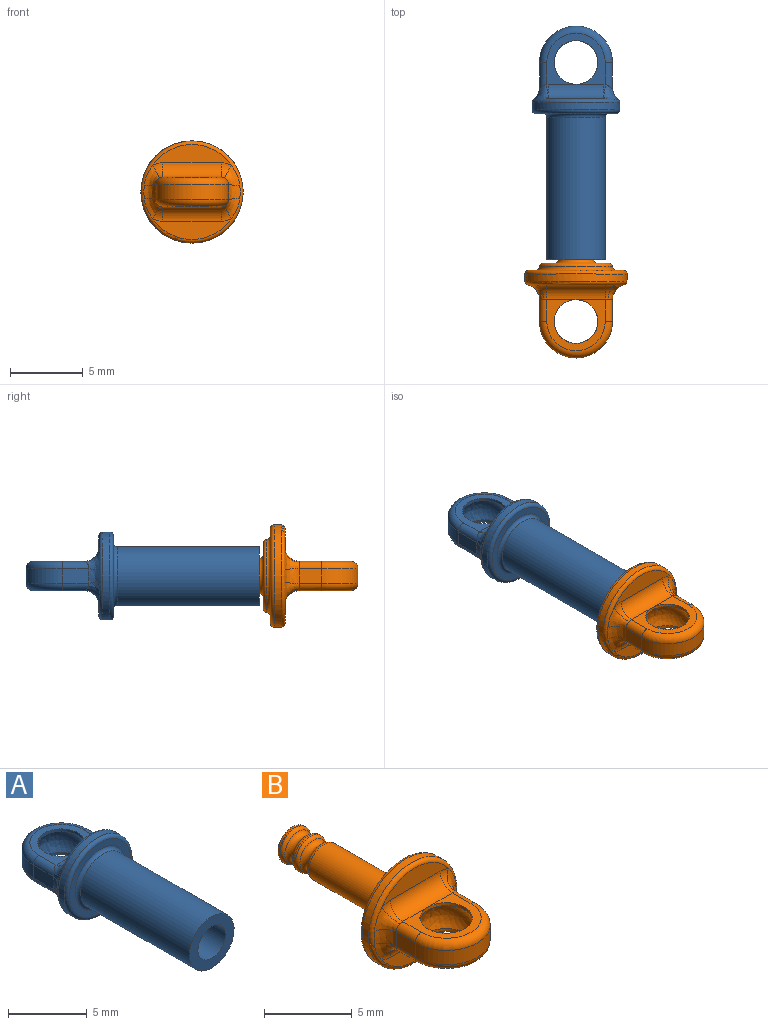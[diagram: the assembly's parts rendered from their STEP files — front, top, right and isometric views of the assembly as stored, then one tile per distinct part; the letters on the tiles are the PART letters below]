
ASSEMBLY  parts=2 mates=1
PART A: 38 faces, bbox 6.5x16.2x6.5 mm
  f0: plane 3.78x0.75mm, normal (0,1,0), area 1.9mm2, adj f23,f35
  f1: cylinder r=1.5mm len=3mm, axis (0,0,-1), area 1.9mm2, adj f7,f8
  f2: plane 1.78x1mm, normal (1,0,0), area 1.8mm2, adj f3,f11,f14,f32
  f3: cylinder r=2.5mm len=5mm, axis (0,0,-1), area 7.9mm2, adj f2,f4,f10,f13
  f4: plane 1.78x1mm, normal (-1,0,0), area 1.8mm2, adj f3,f9,f12,f29
  f5: cylinder r=1.5mm len=3mm, axis (0,0,-1), area 1.9mm2, adj f6,f8
  f6: plane 4x3.5mm, normal (0,0,1), area 5.2mm2, adj f5,f12,f13,f14,f33,f35,f36
  f7: plane 4x3.5mm, normal (0,0,-1), area 5.2mm2, adj f1,f9,f10,f11,f25,f26,f28
  f8: sphere r=1.7mm, area 17.1mm2, adj f1,f5
  f9: cylinder r=0.5mm len=1.78mm, axis (0,-1,0), area 1.3mm2, adj f4,f7,f10,f27
  f10: torus R=2mm, axis (0,0,1), area 5.7mm2, adj f3,f7,f9,f11
  f11: cylinder r=0.5mm len=1.78mm, axis (0,1,0), area 1.3mm2, adj f2,f7,f10,f30
  f12: cylinder r=0.5mm len=1.78mm, axis (0,1,0), area 1.3mm2, adj f4,f6,f13,f31
  f13: torus R=2mm, axis (0,0,1), area 5.7mm2, adj f3,f6,f12,f14
  f14: cylinder r=0.5mm len=1.78mm, axis (0,-1,0), area 1.3mm2, adj f2,f6,f13,f34
  f15: plane 3.78x0.75mm, normal (0,1,0), area 1.9mm2, adj f23,f26
  f16: cylinder r=3mm len=6mm, axis (0,1,0), area 9.4mm2, adj f23,f24
  f17: plane 0.48x0.48mm, normal (0,-1,0), area 0.2mm2, adj f18
  f18: torus R=0.24mm, axis (0,1,0), area 8.7mm2, adj f17,f19
  f19: cylinder r=1.24mm len=9mm, axis (0,1,0), area 70.2mm2, adj f18,f20
  f20: plane 4x4mm, normal (0,-1,0), area 7.7mm2, adj f19,f21
  f21: cylinder r=2mm len=9.75mm, axis (0,1,0), area 122.5mm2, adj f20,f37
  f22: plane 5.5x5.5mm, normal (0,-1,0), area 7.9mm2, adj f24,f37
  f23: torus R=2.75mm, axis (0,-1,0), area 6mm2, adj f0,f15,f16,f25,f27,f28,f29,f30
  f24: torus R=2.75mm, axis (0,1,0), area 7.2mm2, adj f16,f22
  f25: bspline ~1.1x1.1mm, area 0.1mm2, adj f7,f23,f26,f27
  f26: cylinder r=1mm len=3.78mm, axis (1,0,0), area 5.9mm2, adj f7,f15,f25,f28
  f27: bspline ~1.82x1.08mm, area 1.2mm2, adj f9,f23,f25,f29
  f28: bspline ~1.1x1.1mm, area 0.1mm2, adj f7,f23,f26,f30
  f29: bspline ~1.56x0.82mm, area 0.8mm2, adj f4,f23,f27,f31
  f30: bspline ~1.76x1.09mm, area 1.2mm2, adj f11,f23,f28,f32
  f31: bspline ~1.76x1.09mm, area 1.2mm2, adj f12,f23,f29,f33
  f32: bspline ~1.46x0.81mm, area 0.8mm2, adj f2,f23,f30,f34
  f33: bspline ~1.1x1.1mm, area 0.1mm2, adj f6,f23,f31,f35
  f34: bspline ~1.82x1.08mm, area 1.2mm2, adj f14,f23,f32,f36
  f35: cylinder r=1mm len=3.78mm, axis (-1,0,0), area 5.9mm2, adj f0,f6,f33,f36
  f36: bspline ~1.1x1.1mm, area 0.1mm2, adj f6,f23,f34,f35
  f37: torus R=2.25mm, axis (0,1,0), area 5.2mm2, adj f21,f22
PART B: 47 faces, bbox 7.6x15.2x7.6 mm
  f0: cylinder r=1.5mm len=3mm, axis (0,0,-1), area 1.9mm2, adj f22,f46
  f1: plane 5.36x1.41mm, normal (0,-1,0), area 4.5mm2, adj f29,f43,f44,f45
  f2: plane 5.36x1.41mm, normal (0,-1,0), area 4.5mm2, adj f29,f34,f35,f36
  f3: cylinder r=3.5mm len=7mm, axis (0,1,0), area 11mm2, adj f29,f30
  f4: plane 6.5x6.5mm, normal (0,1,0), area 9.4mm2, adj f30,f32
  f5: plane 4.5x4.5mm, normal (0,1,0), area 9.3mm2, adj f31,f33
  f6: cylinder r=1.2mm len=5.62mm, axis (0,1,0), area 42.4mm2, adj f7,f33
  f7: torus R=0.95mm, axis (0,1,0), area 2.1mm2, adj f6,f8
  f8: torus R=1.2mm, axis (0,1,0), area 4.6mm2, adj f7,f9
  f9: torus R=0.95mm, axis (0,1,0), area 2.1mm2, adj f8,f10
  f10: cylinder r=1.2mm len=2.4mm, axis (0,1,0), area 0.9mm2, adj f9,f11
  f11: torus R=0.95mm, axis (0,1,0), area 2.1mm2, adj f10,f12
  f12: torus R=1.2mm, axis (0,1,0), area 4.6mm2, adj f11,f13
  f13: torus R=0.95mm, axis (0,1,0), area 2.1mm2, adj f12,f14
  f14: cylinder r=1.2mm len=2.4mm, axis (0,1,0), area 0.6mm2, adj f13,f15
  f15: torus R=0.95mm, axis (0,1,0), area 2.7mm2, adj f14,f16
  f16: plane 1.9x1.9mm, normal (0,1,0), area 2.8mm2, adj f15
  f17: plane 1.53x1mm, normal (-1,0,0), area 1.5mm2, adj f18,f23,f26,f39
  f18: cylinder r=2.5mm len=5mm, axis (0,0,-1), area 7.9mm2, adj f17,f19,f24,f27
  f19: plane 1.53x1mm, normal (1,0,0), area 1.5mm2, adj f18,f25,f28,f40
  f20: cylinder r=1.5mm len=3mm, axis (0,0,-1), area 1.9mm2, adj f21,f46
  f21: plane 4x3.5mm, normal (0,0,1), area 5.2mm2, adj f20,f26,f27,f28,f34
  f22: plane 4x3.5mm, normal (0,0,-1), area 5.2mm2, adj f0,f23,f24,f25,f45
  f23: cylinder r=0.5mm len=1.53mm, axis (0,-1,0), area 1.2mm2, adj f17,f22,f24,f41,f43
  f24: torus R=2mm, axis (0,0,1), area 5.7mm2, adj f18,f22,f23,f25
  f25: cylinder r=0.5mm len=1.53mm, axis (0,1,0), area 1.2mm2, adj f19,f22,f24,f42,f44
  f26: cylinder r=0.5mm len=1.53mm, axis (0,1,0), area 1.2mm2, adj f17,f21,f27,f35,f37
  f27: torus R=2mm, axis (0,0,1), area 5.7mm2, adj f18,f21,f26,f28
  f28: cylinder r=0.5mm len=1.53mm, axis (0,-1,0), area 1.2mm2, adj f19,f21,f27,f36,f38
  f29: torus R=3.25mm, axis (0,1,0), area 8mm2, adj f1,f2,f3,f37,f38,f39,f40,f41
  f30: torus R=3.25mm, axis (0,-1,0), area 8.4mm2, adj f3,f4
  f31: torus R=2.25mm, axis (0,-1,0), area 5.9mm2, adj f5,f32
  f32: torus R=2.75mm, axis (0,-1,0), area 6.4mm2, adj f4,f31
  f33: torus R=1.45mm, axis (0,-1,0), area 3.2mm2, adj f5,f6
  f34: cylinder r=1mm len=4mm, axis (1,0,0), area 6.3mm2, adj f2,f21,f35,f36
  f35: torus R=1.5mm, axis (0,1,0), area 0.6mm2, adj f2,f26,f34,f37
  f36: torus R=1.5mm, axis (0,1,0), area 0.6mm2, adj f2,f28,f34,f38
  f37: bspline ~1.87x1.16mm, area 1.2mm2, adj f26,f29,f35,f39
  f38: bspline ~1.87x1.16mm, area 1.2mm2, adj f28,f29,f36,f40
  f39: bspline ~1.77x0.99mm, area 1.3mm2, adj f17,f29,f37,f41
  f40: bspline ~1.87x0.99mm, area 1.3mm2, adj f19,f29,f38,f42
  f41: bspline ~1.87x1.16mm, area 1.2mm2, adj f23,f29,f39,f43
  f42: bspline ~1.64x1.15mm, area 1.2mm2, adj f25,f29,f40,f44
  f43: torus R=1.5mm, axis (0,1,0), area 0.6mm2, adj f1,f23,f41,f45
  f44: torus R=1.5mm, axis (0,1,0), area 0.6mm2, adj f1,f25,f42,f45
  f45: cylinder r=1mm len=4mm, axis (-1,0,0), area 6.3mm2, adj f1,f22,f43,f44
  f46: sphere r=1.7mm, area 17.1mm2, adj f0,f20
PLACE A t=(0.19,13.65,-0.21)mm
PLACE B t=(0.19,0.9,-0.21)mm
MATE slider A.f24 <-> B.f3  axis (0,1,0) through (0.19,2.65,-0.21)mm
